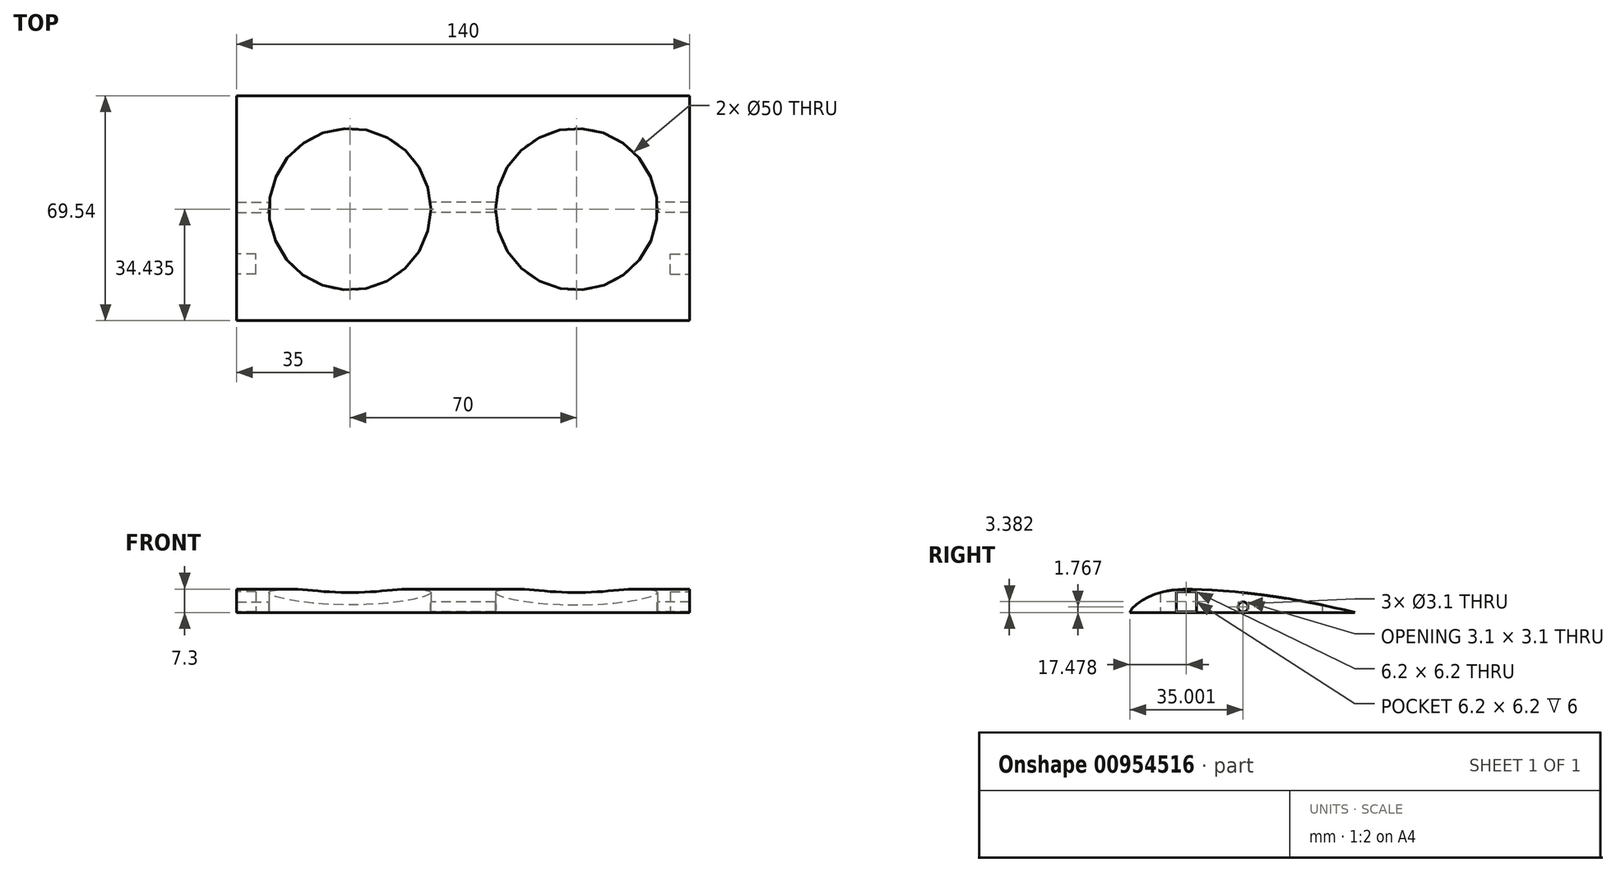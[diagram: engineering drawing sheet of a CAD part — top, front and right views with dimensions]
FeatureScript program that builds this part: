
annotation { "Feature Type Name" : "Feature", "Feature Type Description" : "" }
export const myFeature = defineFeature(function(context is Context, id is Id, definition is map)
    precondition{}
    {
        {
            var Q0;
            Q0=qCreatedBy(makeId("Right.planeOp"),FACE);
            var sketch = newSketch(context, id + "F0", { "sketchPlane" : qUnion([Q0])});
            skLineSegment(sketch, "E0", {"start": v(-47.02, 44.82) * mm, "end": v(22.98, 44.82) * mm, "construction": true});
            skFitSpline(sketch, "E1", {"points": [v(-45.36, 32.1) * mm, v(-44.32, 33.79) * mm, v(-41.19, 36.12) * mm, v(-37.17, 37.96) * mm, v(-29.8, 39.33) * mm, v(-22.09, 39.17) * mm, v(-11.01, 38.36) * mm, v(4.48, 36.28) * mm, v(15.47, 34.2) * mm, v(24.62, 32.1) * mm], "startDerivative": vector(13.81, 29.31) * mm, "endDerivative": vector(73.04, -17.16) * mm});
            skLineSegment(sketch, "E2", {"start": v(24.18, 32.1) * mm, "end": v(-45.36, 32.1) * mm});
            skLineSegment(sketch, "E3", {"start": v(24.18, 32.1) * mm, "end": v(24.07, 32.23) * mm});
            skSolve(sketch);
        }
        {
            var Q0;
            Q0=makeQuery(id+"F0.imprint","IMPRINT",FACE,{"disambiguationData":[TD([[makeQuery(id+"F0.imprint","IMPRINT",EDGE,{"derivedFrom":sQuery(id+"F0.wireOp",EDGE,"E1")}),-1.0]])]});
            extrude(context, id + "F1", {"entities" : qUnion([Q0]), "depth" : 70 * mm, "offsetDistance" : 25 * mm});
        }
        {
            var Q0;
            Q0=qCreatedBy(makeId("Top.planeOp"),FACE);
            var sketch = newSketch(context, id + "F2", { "sketchPlane" : qUnion([Q0])});
            skLineSegment(sketch, "E4.bottom", {"start": v(0, 24.07) * mm, "end": v(70, 24.07) * mm});
            skLineSegment(sketch, "E4.top", {"start": v(0, -45.93) * mm, "end": v(70, -45.93) * mm});
            skLineSegment(sketch, "E4.left", {"start": v(0, 24.07) * mm, "end": v(0, -45.93) * mm});
            skLineSegment(sketch, "E4.right", {"start": v(70, 24.07) * mm, "end": v(70, -45.93) * mm});
            skPoint(sketch, "E5", {"position": v(35, -10.93) * mm});
            skPoint(sketch, "E5.positionSnap0", {"position": v(70, -10.93) * mm});
            skPoint(sketch, "E5.positionSnap1", {"position": v(35, 24.07) * mm});
            skCircle(sketch, "E6", {"center": v(35, -10.93) * mm, "radius": 25 * mm});
            skSolve(sketch);
        }
        {
            var Q0;
            Q0=makeQuery(id+"F2.imprint","IMPRINT",FACE,{"disambiguationData":[TD([[makeQuery(id+"F2.imprint","IMPRINT",EDGE,{"derivedFrom":sQuery(id+"F2.wireOp",EDGE,"E6")}),1.0]])]});
            extrude(context, id + "F3", {"entities" : qUnion([Q0]), "operationType" : NewBodyOperationType.REMOVE, "depth" : 72.1 * mm, "offsetDistance" : 25 * mm});
        }
        {
            var Q0;
            Q0=makeQuery(id+"F1.opExtrude","CAP_FACE",FACE,{"disambiguationData":[OSD([sQuery(id+"F0.wireOp",EDGE,"E1"),sQuery(id+"F0.wireOp",EDGE,"E2"),sQuery(id+"F0.wireOp",EDGE,"E3")])],"isStart":false});
            var sketch = newSketch(context, id + "F4", { "sketchPlane" : qUnion([Q0])});
            skLineSegment(sketch, "E7.bottom", {"start": v(-30.98, 38.58) * mm, "end": v(-24.78, 38.58) * mm});
            skLineSegment(sketch, "E7.top", {"start": v(-30.98, 32.38) * mm, "end": v(-24.78, 32.38) * mm});
            skLineSegment(sketch, "E7.left", {"start": v(-30.98, 38.58) * mm, "end": v(-30.98, 32.38) * mm});
            skLineSegment(sketch, "E7.right", {"start": v(-24.78, 38.58) * mm, "end": v(-24.78, 32.38) * mm});
            skSolve(sketch);
        }
        {
            var Q0;
            Q0=makeQuery(id+"F4.imprint","IMPRINT",FACE,{"disambiguationData":[TD([[makeQuery(id+"F4.imprint","IMPRINT",EDGE,{"derivedFrom":sQuery(id+"F4.wireOp",EDGE,"E7.bottom")}),-1.0]])]});
            extrude(context, id + "F5", {"entities" : qUnion([Q0]), "operationType" : NewBodyOperationType.REMOVE, "oppositeDirection" : true, "depth" : 6 * mm, "offsetDistance" : 25 * mm});
        }
        {
            var Q0;
            Q0=qCreatedBy(makeId("Right.planeOp"),FACE);
            var sketch = newSketch(context, id + "F6", { "sketchPlane" : qUnion([Q0])});
            skLineSegment(sketch, "E8", {"start": v(-45.36, 32.1) * mm, "end": v(24.64, 32.1) * mm, "construction": true});
            skCircle(sketch, "E9", {"center": v(-10.36, 33.87) * mm, "radius": 1.55 * mm});
            skPoint(sketch, "E9.centerSnap0", {"position": v(-10.36, 32.1) * mm});
            skSolve(sketch);
        }
        {
            var Q0;
            Q0=makeQuery(id+"F6.imprint","IMPRINT",FACE,{"disambiguationData":[TD([[makeQuery(id+"F6.imprint","IMPRINT",EDGE,{"derivedFrom":sQuery(id+"F6.wireOp",EDGE,"E9")}),1.0]])]});
            extrude(context, id + "F7", {"entities" : qUnion([Q0]), "operationType" : NewBodyOperationType.REMOVE, "depth" : 77.3 * mm, "offsetDistance" : 25 * mm});
        }
        {
            var Q0;
            Q0=makeQuery(id+"F1.opExtrude","SWEPT_BODY",BODY,{"disambiguationData":[OSD([sQuery(id+"F0.wireOp",EDGE,"E1"),sQuery(id+"F0.wireOp",EDGE,"E2"),sQuery(id+"F0.wireOp",EDGE,"E3")])]});
            var Q1;
            Q1=qCreatedBy(makeId("Right.planeOp"),FACE);
            mirror(context, id + "F8", {"operationType" : NewBodyOperationType.ADD, "entities" : qUnion([Q0]), "mirrorPlane" : qUnion([Q1])});
        }
    });
